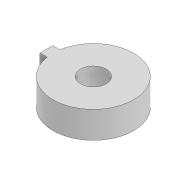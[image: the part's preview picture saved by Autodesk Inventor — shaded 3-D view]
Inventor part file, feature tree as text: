
AUTODESK INVENTOR PART (.ipt)
format: ipt  version: 2022 (Build 260153000, 153)  size: 92,160 bytes
history: native  units: mm
features: extrude x1, sketch x1
ambient origin geometry x8: Origin, YZ Plane, XZ Plane, XY Plane, X Axis, Y Axis, Z Axis, Center Point
bodies: Solid1 (feature_tree)
feature tree (2):
  extrude  "Extrusion1"  Depth=10.0mm
  sketch  "Sketch1"  dims[d0=30.0mm d1=9.534878mm d2=10.0mm d3=0.0mm]
